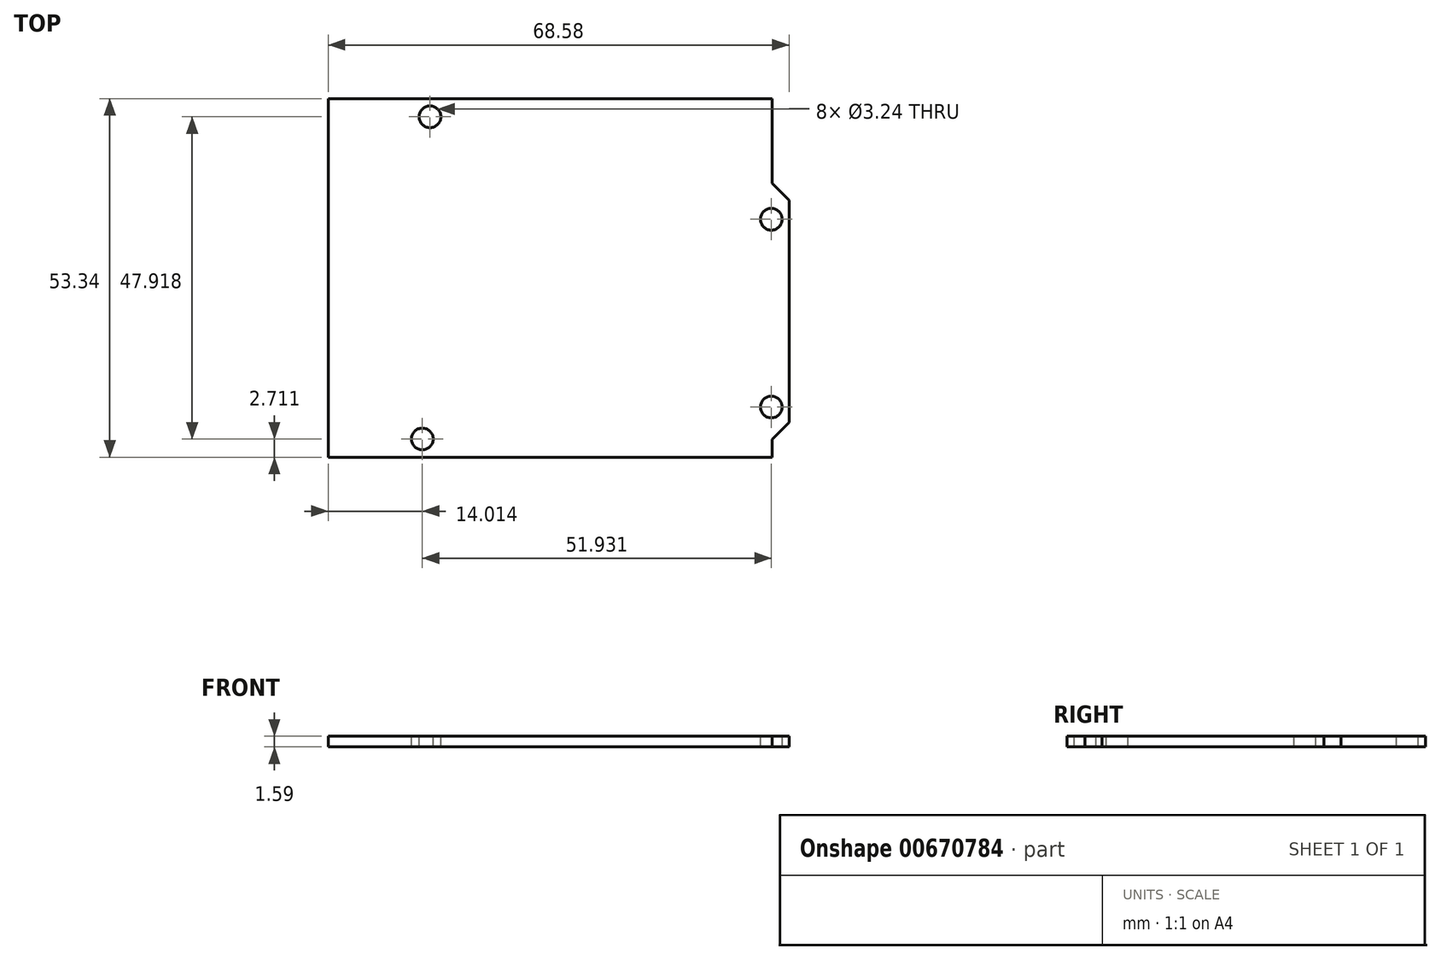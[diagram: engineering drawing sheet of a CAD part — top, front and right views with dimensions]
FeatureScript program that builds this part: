
annotation { "Feature Type Name" : "Feature", "Feature Type Description" : "" }
export const myFeature = defineFeature(function(context is Context, id is Id, definition is map)
    precondition{}
    {
        {
            var Q0;
            Q0=qCreatedBy(makeId("Top.planeOp"),FACE);
            var sketch = newSketch(context, id + "F0", { "sketchPlane" : qUnion([Q0])});
            skLineSegment(sketch, "E0", {"start": v(-33.02, 26.67) * mm, "end": v(33.02, 26.67) * mm});
            skLineSegment(sketch, "E1", {"start": v(33.02, -26.67) * mm, "end": v(-33.02, -26.67) * mm});
            skLineSegment(sketch, "E2", {"start": v(-33.02, -26.67) * mm, "end": v(-33.02, 26.67) * mm});
            skLineSegment(sketch, "E3", {"start": v(0, 0) * mm, "end": v(0, 26.67) * mm, "construction": true});
            skLineSegment(sketch, "E4", {"start": v(0, 0) * mm, "end": v(0, -26.67) * mm, "construction": true});
            skLineSegment(sketch, "E5", {"start": v(0, 0) * mm, "end": v(-33.02, 0) * mm, "construction": true});
            skLineSegment(sketch, "E6", {"start": v(0, 0) * mm, "end": v(33.02, 0) * mm, "construction": true});
            skLineSegment(sketch, "E7", {"start": v(33.02, -24) * mm, "end": v(35.56, -21.46) * mm});
            skLineSegment(sketch, "E8", {"start": v(35.56, -21.46) * mm, "end": v(35.56, 11.56) * mm});
            skLineSegment(sketch, "E9", {"start": v(35.56, 11.56) * mm, "end": v(33.02, 14.1) * mm});
            skLineSegment(sketch, "E10", {"start": v(33.02, -26.67) * mm, "end": v(33.02, -24) * mm});
            skLineSegment(sketch, "E11", {"start": v(33.02, 14.1) * mm, "end": v(33.02, 26.67) * mm});
            skSolve(sketch);
        }
        {
            var Q0;
            Q0=makeQuery(id+"F0.imprint","IMPRINT",FACE,{"disambiguationData":[TD([[makeQuery(id+"F0.imprint","IMPRINT",EDGE,{"derivedFrom":sQuery(id+"F0.wireOp",EDGE,"E0")}),-1.0]])]});
            extrude(context, id + "F1", {"entities" : qUnion([Q0]), "depth" : 1.59 * mm, "offsetDistance" : 25 * mm});
        }
        {
            var Q0;
            Q0=makeQuery(id+"F1.opExtrude","CAP_FACE",FACE,{"disambiguationData":[OSD([sQuery(id+"F0.wireOp",EDGE,"E0"),sQuery(id+"F0.wireOp",EDGE,"E1"),sQuery(id+"F0.wireOp",EDGE,"E2"),sQuery(id+"F0.wireOp",EDGE,"E7"),sQuery(id+"F0.wireOp",EDGE,"E8"),sQuery(id+"F0.wireOp",EDGE,"E9"),sQuery(id+"F0.wireOp",EDGE,"E10"),sQuery(id+"F0.wireOp",EDGE,"E11")])],"isStart":false});
            var sketch = newSketch(context, id + "F2", { "sketchPlane" : qUnion([Q0])});
            skCircle(sketch, "E12", {"center": v(-17.86, 23.96) * mm, "radius": 1.62 * mm});
            skCircle(sketch, "E13", {"center": v(32.93, 8.72) * mm, "radius": 1.62 * mm});
            skCircle(sketch, "E14", {"center": v(-19, -23.96) * mm, "radius": 1.62 * mm});
            skCircle(sketch, "E15", {"center": v(32.93, -19.2) * mm, "radius": 1.62 * mm});
            skSolve(sketch);
        }
        {
            var Q0;
            Q0=makeQuery(id+"F2.imprint","IMPRINT",FACE,{"disambiguationData":[TD([[makeQuery(id+"F2.imprint","IMPRINT",EDGE,{"derivedFrom":sQuery(id+"F2.wireOp",EDGE,"E12")}),1.0]])]});
            var Q1;
            Q1=makeQuery(id+"F2.imprint","IMPRINT",FACE,{"disambiguationData":[TD([[makeQuery(id+"F2.imprint","IMPRINT",EDGE,{"derivedFrom":sQuery(id+"F2.wireOp",EDGE,"E14")}),1.0]])]});
            var Q2;
            Q2=makeQuery(id+"F2.imprint","IMPRINT",FACE,{"disambiguationData":[TD([[makeQuery(id+"F2.imprint","IMPRINT",EDGE,{"derivedFrom":sQuery(id+"F2.wireOp",EDGE,"E15")}),1.0]])]});
            var Q3;
            Q3=makeQuery(id+"F2.imprint","IMPRINT",FACE,{"disambiguationData":[TD([[makeQuery(id+"F2.imprint","IMPRINT",EDGE,{"derivedFrom":sQuery(id+"F2.wireOp",EDGE,"E13")}),1.0]])]});
            extrude(context, id + "F3", {"entities" : qUnion([Q0, Q1, Q2, Q3]), "operationType" : NewBodyOperationType.REMOVE, "oppositeDirection" : true, "depth" : 25 * mm, "offsetDistance" : 25 * mm});
        }
    });
